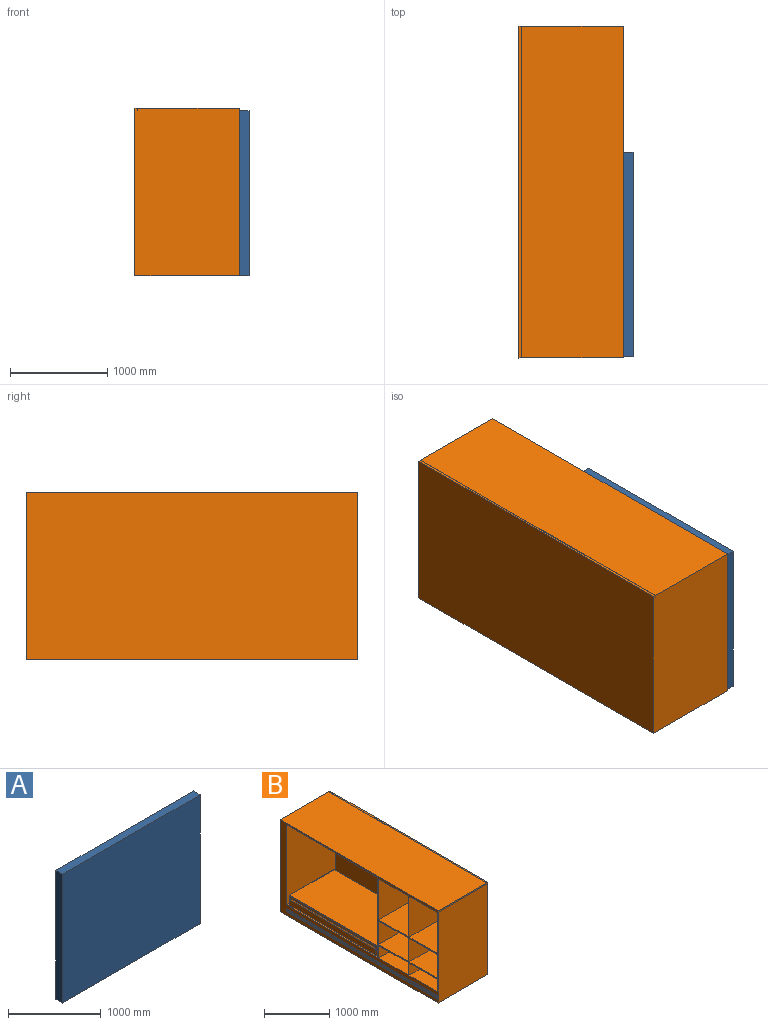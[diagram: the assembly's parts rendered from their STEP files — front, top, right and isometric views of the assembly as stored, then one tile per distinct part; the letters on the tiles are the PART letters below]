
ASSEMBLY  parts=2 mates=2
PART A: 6 faces, bbox 2100x100x1700 mm
  f0: plane 2100x1700mm, normal (0,1,0), area 3570000mm2, adj f1,f3,f4,f5
  f1: plane 1700x100mm, normal (-1,0,0), area 170000mm2, adj f0,f2,f4,f5
  f2: plane 2100x1700mm, normal (0,-1,0), area 3570000mm2, adj f1,f3,f4,f5
  f3: plane 1700x100mm, normal (1,0,0), area 170000mm2, adj f0,f2,f4,f5
  f4: plane 2100x100mm, normal (0,0,1), area 210000mm2, adj f0,f1,f2,f3
  f5: plane 2100x100mm, normal (0,0,-1), area 210000mm2, adj f0,f1,f2,f3
PART B: 94 faces, bbox 1080x3415.1x1725 mm
  f0: plane 763.79x630mm, normal (-1,0,0), area 481187.5mm2, adj f71,f73,f74,f93
  f1: plane 1019x763.79mm, normal (0,1,0), area 775969.2mm2, adj f2,f13,f79,f84,f90
  f2: plane 763.79x610mm, normal (-1,0,0), area 465911.7mm2, adj f1,f76,f79,f90
  f3: plane 1019x441.31mm, normal (0,-1,0), area 449692.9mm2, adj f6,f13,f88,f92
  f4: plane 1019x441.31mm, normal (0,1,0), area 449692.9mm2, adj f6,f13,f88,f92
  f5: plane 1019x441.31mm, normal (0,-1,0), area 449692.9mm2, adj f8,f13,f86,f91
  f6: plane 630x441.31mm, normal (-1,0,0), area 278024.1mm2, adj f3,f4,f88,f92
  f7: plane 1019x441.31mm, normal (0,1,0), area 449692.9mm2, adj f8,f13,f86,f91
  f8: plane 610x441.31mm, normal (-1,0,0), area 269197.9mm2, adj f5,f7,f86,f91
  f9: plane 1019x232.38mm, normal (0,-1,0), area 236797.7mm2, adj f13,f72,f75,f89
  f10: plane 1019x232.38mm, normal (0,1,0), area 236797.7mm2, adj f13,f72,f75,f89
  f11: plane 1019x232.38mm, normal (0,-1,0), area 236797.7mm2, adj f13,f77,f80,f87
  f12: plane 137x1.45mm, normal (0,0,1), area 198.3mm2, adj f15,f19,f20,f83
  f13: plane 3415.14x1725mm, normal (-1,0,0), area 1088941.3mm2, adj f1,f3,f4,f5,f7,f9,f10,f11
  f14: plane 3415.14x1075mm, normal (0,0,-1), area 3671270.9mm2, adj f13,f18,f69,f83
  f15: plane 3414.78x25mm, normal (1,0,0), area 85369.5mm2, adj f12,f16,f21,f81,f82,f83
  f16: plane 3414.78x1048.55mm, normal (0,0,1), area 3580578.9mm2, adj f13,f15,f81,f83
  f17: plane 3415.14x25mm, normal (0,0,1), area 85378.4mm2, adj f18,f19,f69,f83
  f18: plane 3415.14x1724.51mm, normal (1,0,0), area 5889440.8mm2, adj f14,f17,f69,f83
  f19: plane 3415.14x1524.51mm, normal (-1,0,0), area 3050913.7mm2, adj f12,f17,f20,f21,f22,f69,f70,f83
  f20: plane 1500x1050mm, normal (0,-1,0), area 1575000mm2, adj f12,f13,f19,f22,f82
  f21: plane 1300x1050mm, normal (0,0,1), area 2252.7mm2, adj f13,f15,f19,f69,f70,f81
  f22: plane 1978.14x1050mm, normal (0,0,1), area 123979.4mm2, adj f13,f19,f20,f23,f24,f25,f26,f27
  f23: plane 1855.15x100mm, normal (-1,0,0), area 185514.7mm2, adj f22,f27,f30,f36
  f24: plane 905.15x100mm, normal (0,-1,0), area 90514.7mm2, adj f22,f27,f28,f37
  f25: plane 1855.15x100mm, normal (1,0,0), area 185514.7mm2, adj f22,f28,f29,f33
  f26: plane 905.15x100mm, normal (0,1,0), area 90514.7mm2, adj f22,f29,f30,f32
  f27: cylinder r=48.28mm len=100mm, axis (0,0,-1), area 7584.5mm2, adj f22,f23,f24,f38
  f28: cylinder r=48.28mm len=100mm, axis (0,0,1), area 7584.5mm2, adj f22,f24,f25,f35
  f29: cylinder r=48.28mm len=100mm, axis (0,0,-1), area 7584.5mm2, adj f22,f25,f26,f31
  f30: cylinder r=48.28mm len=100mm, axis (0,0,1), area 7584.5mm2, adj f22,f23,f26,f34
  f31: torus R=28.28mm, axis (0,0,1), area 2024.1mm2, adj f29,f32,f33,f39
  f32: cylinder r=20mm len=905.15mm, axis (1,0,0), area 28436mm2, adj f26,f31,f34,f39
  f33: cylinder r=20mm len=1855.15mm, axis (0,-1,0), area 58281.2mm2, adj f25,f31,f35,f39
  f34: torus R=28.28mm, axis (0,0,1), area 2024.1mm2, adj f30,f32,f36,f39
  f35: torus R=28.28mm, axis (0,0,1), area 2024.1mm2, adj f28,f33,f37,f39
  f36: cylinder r=20mm len=1855.15mm, axis (0,1,0), area 58281.2mm2, adj f23,f34,f38,f39
  f37: cylinder r=20mm len=905.15mm, axis (-1,0,0), area 28436mm2, adj f24,f35,f38,f39
  f38: torus R=28.28mm, axis (0,0,1), area 2024.1mm2, adj f27,f36,f37,f39
  f39: plane 1923.48x973.41mm, normal (0,0,-1), area 34400.8mm2, adj f31,f32,f33,f34,f35,f36,f37,f38
  f40: plane 1903.48x40mm, normal (-1,0,0), area 76139.3mm2, adj f39,f45,f48,f54
  f41: plane 953.41x40mm, normal (0,-1,0), area 38136.2mm2, adj f39,f45,f46,f55
  f42: plane 1903.48x40mm, normal (1,0,0), area 76139.3mm2, adj f39,f46,f47,f51
  f43: plane 953.41x40mm, normal (0,1,0), area 38136.2mm2, adj f39,f47,f48,f50
  f44: plane 1903.48x953.41mm, normal (0,0,1), area 1814789.2mm2, adj f50,f51,f54,f55
  f45: cylinder r=10mm len=40mm, axis (0,0,-1), area 628.3mm2, adj f39,f40,f41,f56
  f46: cylinder r=10mm len=40mm, axis (0,0,1), area 628.3mm2, adj f39,f41,f42,f53
  f47: cylinder r=10mm len=40mm, axis (0,0,-1), area 628.3mm2, adj f39,f42,f43,f49
  f48: cylinder r=10mm len=40mm, axis (0,0,1), area 628.3mm2, adj f39,f40,f43,f52
  f49: sphere r=10mm, area 157.1mm2, adj f47,f50,f51
  f50: cylinder r=10mm len=953.41mm, axis (1,0,0), area 14976.1mm2, adj f43,f44,f49,f52
  f51: cylinder r=10mm len=1903.48mm, axis (0,-1,0), area 29899.8mm2, adj f42,f44,f49,f53
  f52: sphere r=10mm, area 157.1mm2, adj f48,f50,f54
  f53: sphere r=10mm, area 157.1mm2, adj f46,f51,f55
  f54: cylinder r=10mm len=1903.48mm, axis (0,1,0), area 29899.8mm2, adj f40,f44,f52,f56
  f55: cylinder r=10mm len=953.41mm, axis (-1,0,0), area 14976.1mm2, adj f41,f44,f53,f56
  f56: sphere r=10mm, area 157.1mm2, adj f45,f54,f55
  f57: plane 3280x5mm, normal (0,0,1), area 16400mm2, adj f13,f58,f60,f69
  f58: plane 5x5mm, normal (0,1,0), area 25mm2, adj f13,f57,f59,f60
  f59: plane 3280x5mm, normal (0,0,-1), area 16400mm2, adj f13,f58,f60,f69
  f60: plane 3280x5mm, normal (-1,0,0), area 16400mm2, adj f57,f58,f59,f69
  f61: plane 3280x5mm, normal (0,0,-1), area 16400mm2, adj f13,f63,f64,f69
  f62: plane 3280x5mm, normal (0,0,1), area 16400mm2, adj f13,f63,f64,f69
  f63: plane 5x5mm, normal (0,1,0), area 25mm2, adj f13,f61,f62,f64
  f64: plane 3280x5mm, normal (-1,0,0), area 16400mm2, adj f61,f62,f63,f69
  f65: plane 3280x5mm, normal (0,0,1), area 16400mm2, adj f13,f66,f68,f69
  f66: plane 6x5mm, normal (0,1,0), area 30mm2, adj f13,f65,f67,f68
  f67: plane 3280x5mm, normal (0,0,-1), area 16400mm2, adj f13,f66,f68,f69
  f68: plane 3280x6mm, normal (-1,0,0), area 19680mm2, adj f65,f66,f67,f69
  f69: plane 1724.51x1080mm, normal (0,-1,0), area 1828192.8mm2, adj f13,f14,f17,f18,f19,f21,f57,f59
  f70: plane 1500x1050mm, normal (0,1,0), area 1575000mm2, adj f13,f19,f21,f22,f82
  f71: plane 1019x763.79mm, normal (0,-1,0), area 775969.2mm2, adj f0,f13,f74,f85,f93
  f72: plane 1019x630mm, normal (0,0,1), area 641970mm2, adj f9,f10,f13,f75
  f73: plane 1019x763.79mm, normal (0,1,0), area 775969.2mm2, adj f0,f13,f74,f85,f93
  f74: plane 1019x630mm, normal (0,0,-1), area 641970mm2, adj f0,f13,f71,f73
  f75: plane 630x232.38mm, normal (-1,0,0), area 146400.9mm2, adj f9,f10,f72,f89
  f76: plane 1019x763.79mm, normal (0,-1,0), area 775969.2mm2, adj f2,f13,f79,f84,f90
  f77: plane 1019x610mm, normal (0,0,1), area 621590mm2, adj f11,f13,f78,f80
  f78: plane 1019x232.38mm, normal (0,1,0), area 236797.7mm2, adj f13,f77,f80,f87
  f79: plane 1019x610mm, normal (0,0,-1), area 621590mm2, adj f1,f2,f13,f76
  f80: plane 610x232.38mm, normal (-1,0,0), area 141753.3mm2, adj f11,f77,f78,f87
  f81: plane 1048.55x25mm, normal (0,-1,0), area 26213.8mm2, adj f13,f15,f16,f21
  f82: plane 1978.14x1048.55mm, normal (0,0,-1), area 2074179.9mm2, adj f13,f15,f20,f70
  f83: plane 1725x1075mm, normal (0,1,0), area 1854326.6mm2, adj f12,f13,f14,f15,f16,f17,f18,f19
  f84: cylinder r=27.25mm len=610mm, axis (0,-1,0), area 104433.6mm2, adj f1,f76
  f85: cylinder r=27.25mm len=630mm, axis (0,-1,0), area 107857.7mm2, adj f71,f73
  f86: plane 1019x610mm, normal (0,0,1), area 621590mm2, adj f5,f7,f8,f13
  f87: plane 1019x610mm, normal (0,0,-1), area 621590mm2, adj f11,f13,f78,f80
  f88: plane 1019x630mm, normal (0,0,1), area 641970mm2, adj f3,f4,f6,f13
  f89: plane 1019x630mm, normal (0,0,-1), area 641970mm2, adj f9,f10,f13,f75
  f90: plane 1019x610mm, normal (0,0,1), area 621590mm2, adj f1,f2,f13,f76
  f91: plane 1019x610mm, normal (0,0,-1), area 621590mm2, adj f5,f7,f8,f13
  f92: plane 1019x630mm, normal (0,0,-1), area 641970mm2, adj f3,f4,f6,f13
  f93: plane 1019x630mm, normal (0,0,1), area 641970mm2, adj f0,f13,f71,f73
PLACE A rot(axis=(0,0,-1),90deg) t=(-836.95,1465.49,569.3)mm
PLACE B rot(axis=(0,0,-1),180deg) t=(-845.13,1530.55,569.3)mm
MATE slider A.f1 <-> B.f70  axis (0,1,0) through (-745.13,1530.55,2269.3)mm
MATE slider A.f3 <-> A.f3  axis (0,-1,0) through (-745.13,-569.45,569.3)mm
